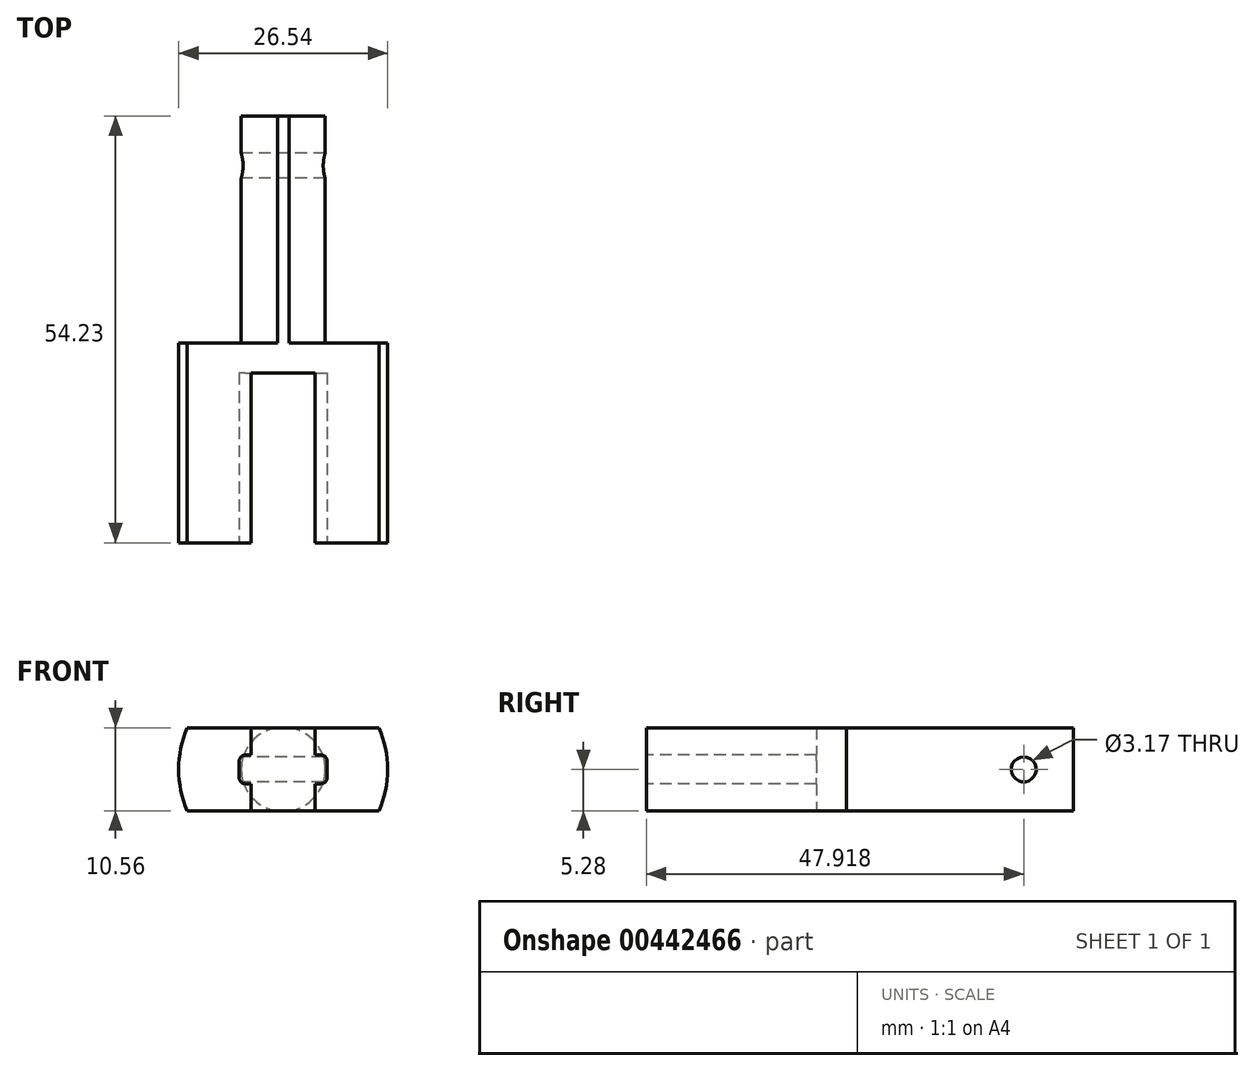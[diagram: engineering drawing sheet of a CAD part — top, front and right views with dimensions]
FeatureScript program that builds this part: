
annotation { "Feature Type Name" : "Feature", "Feature Type Description" : "" }
export const myFeature = defineFeature(function(context is Context, id is Id, definition is map)
    precondition{}
    {
        {
            var Q0;
            Q0=qCreatedBy(makeId("Front.planeOp"),FACE);
            var sketch = newSketch(context, id + "F0", { "sketchPlane" : qUnion([Q0])});
            skCircle(sketch, "E0", {"center": v(0, 0) * mm, "radius": 5.33 * mm});
            skSolve(sketch);
        }
        {
            var Q0;
            Q0 = qSketchRegion(id + "F0", true);
            extrude(context, id + "F1", {"entities" : qUnion([Q0]), "depth" : 28.83 * mm});
        }
        {
            var Q0;
            Q0=makeQuery(id+"F1.opExtrude","CAP_FACE",FACE,{"disambiguationData":[OSD([sQuery(id+"F0.wireOp",EDGE,"E0")])],"isStart":false});
            var sketch = newSketch(context, id + "F2", { "sketchPlane" : qUnion([Q0])});
            skCircle(sketch, "E1", {"center": v(0, 0) * mm, "radius": 13.27 * mm});
            skSolve(sketch);
        }
        {
            var Q0;
            Q0 = qSketchRegion(id + "F2", true);
            extrude(context, id + "F3", {"entities" : qUnion([Q0]), "operationType" : NewBodyOperationType.ADD, "depth" : 25.4 * mm});
        }
        {
            var Q0;
            Q0=makeQuery(id+"F3.opExtrude","CAP_FACE",FACE,{"disambiguationData":[OSD([sQuery(id+"F2.wireOp",EDGE,"E1")])],"isStart":false});
            var sketch = newSketch(context, id + "F4", { "sketchPlane" : qUnion([Q0])});
            skLineSegment(sketch, "E2.bottom", {"start": v(-13.27, 5.28) * mm, "end": v(13.27, 5.28) * mm});
            skLineSegment(sketch, "E2.top", {"start": v(-13.27, -5.28) * mm, "end": v(13.27, -5.28) * mm});
            skLineSegment(sketch, "E2.left", {"start": v(-13.27, 5.28) * mm, "end": v(-13.27, -5.28) * mm});
            skLineSegment(sketch, "E2.right", {"start": v(13.27, 5.28) * mm, "end": v(13.27, -5.28) * mm});
            skPoint(sketch, "E2.middle", {"position": v(0, 0) * mm});
            skSolve(sketch);
        }
        {
            var Q0;
            Q0 = qSketchRegion(id + "F4", true);
            extrude(context, id + "F5", {"entities" : qUnion([Q0]), "operationType" : NewBodyOperationType.INTERSECT, "endBound" : BoundingType.UP_TO_NEXT, "oppositeDirection" : true, "depth" : 25.4 * mm});
        }
        {
            var Q0;
            Q0=makeQuery(id+"F3.opExtrude","CAP_FACE",FACE,{"disambiguationData":[OSD([sQuery(id+"F2.wireOp",EDGE,"E1")])],"isStart":false});
            var sketch = newSketch(context, id + "F6", { "sketchPlane" : qUnion([Q0])});
            skLineSegment(sketch, "E3.bottom", {"start": v(-4.06, 5.28) * mm, "end": v(4.06, 5.28) * mm});
            skLineSegment(sketch, "E3.top", {"start": v(-4.06, -5.28) * mm, "end": v(4.06, -5.28) * mm});
            skLineSegment(sketch, "E3.left", {"start": v(-4.06, 5.28) * mm, "end": v(-4.06, -5.28) * mm});
            skLineSegment(sketch, "E3.right", {"start": v(4.06, 5.28) * mm, "end": v(4.06, -5.28) * mm});
            skPoint(sketch, "E3.middle", {"position": v(0, 0) * mm});
            skSolve(sketch);
        }
        {
            var Q0;
            Q0 = qSketchRegion(id + "F6", true);
            extrude(context, id + "F7", {"entities" : qUnion([Q0]), "operationType" : NewBodyOperationType.REMOVE, "oppositeDirection" : true, "depth" : 21.59 * mm});
        }
        {
            var Q0;
            {var subQ0=sQuery(id+"F2.wireOp",EDGE,"E1");Q0=makeQuery(id+"F7.boolean.opBoolean","SPLIT",FACE,{"disambiguationData":[TD([makeQuery(id+"F7.opExtrude","SWEPT_FACE",FACE,{"disambiguationData":[OSD([sQuery(id+"F6.wireOp",EDGE,"E3.left")])]})])],"derivedFrom":makeQuery(id+"F3.opExtrude","CAP_FACE",FACE,{"disambiguationData":[OSD([subQ0])],"isStart":false})});}
            var sketch = newSketch(context, id + "F8", { "sketchPlane" : qUnion([Q0])});
            skLineSegment(sketch, "E4.bottom", {"start": v(-4.83, 1.81) * mm, "end": v(4.83, 1.81) * mm});
            skLineSegment(sketch, "E4.top", {"start": v(-4.83, -1.81) * mm, "end": v(4.83, -1.81) * mm});
            skLineSegment(sketch, "E4.left", {"start": v(-5.59, 1.05) * mm, "end": v(-5.59, -1.05) * mm});
            skLineSegment(sketch, "E4.right", {"start": v(5.59, 1.05) * mm, "end": v(5.59, -1.05) * mm});
            skPoint(sketch, "E4.middle", {"position": v(0, 0) * mm});
            skPoint(sketch, "E5.visualSharp", {"position": v(-5.59, 1.81) * mm});
            skArc(sketch, "E5.filletArc", {"start": v(-4.83, 1.81) * mm, "mid": v(-5.36, 1.59) * mm, "end": v(-5.59, 1.05) * mm});
            skPoint(sketch, "E6.visualSharp", {"position": v(-5.59, -1.81) * mm});
            skArc(sketch, "E6.filletArc", {"start": v(-5.59, -1.05) * mm, "mid": v(-5.36, -1.59) * mm, "end": v(-4.83, -1.81) * mm});
            skPoint(sketch, "E7.visualSharp", {"position": v(5.59, -1.81) * mm});
            skArc(sketch, "E7.filletArc", {"start": v(4.83, -1.81) * mm, "mid": v(5.36, -1.59) * mm, "end": v(5.59, -1.05) * mm});
            skPoint(sketch, "E8.visualSharp", {"position": v(5.59, 1.81) * mm});
            skArc(sketch, "E8.filletArc", {"start": v(5.59, 1.05) * mm, "mid": v(5.36, 1.59) * mm, "end": v(4.83, 1.81) * mm});
            skSolve(sketch);
        }
        {
            var Q0;
            Q0 = qSketchRegion(id + "F8", true);
            extrude(context, id + "F9", {"entities" : qUnion([Q0]), "operationType" : NewBodyOperationType.REMOVE, "oppositeDirection" : true, "depth" : 21.59 * mm});
        }
        {
            var Q0;
            Q0 = qSketchRegion(id + "F8", true);
            extrude(context, id + "F10", {"entities" : qUnion([Q0]), "operationType" : NewBodyOperationType.REMOVE, "oppositeDirection" : true, "depth" : 21.59 * mm});
        }
        {
            var Q0;
            Q0=qCreatedBy(makeId("Right.planeOp"),FACE);
            var sketch = newSketch(context, id + "F11", { "sketchPlane" : qUnion([Q0])});
            skCircle(sketch, "E9", {"center": v(-6.31, 0) * mm, "radius": 1.59 * mm});
            skSolve(sketch);
        }
        {
            var Q0;
            Q0 = qSketchRegion(id + "F11", true);
            extrude(context, id + "F12", {"entities" : qUnion([Q0]), "operationType" : NewBodyOperationType.REMOVE, "endBound" : BoundingType.UP_TO_NEXT, "depth" : 25.4 * mm, "hasSecondDirection" : true, "secondDirectionBound" : SecondDirectionBoundingType.UP_TO_NEXT, "secondDirectionOppositeDirection" : true, "secondDirectionDepth" : 25.4 * mm});
        }
    });
